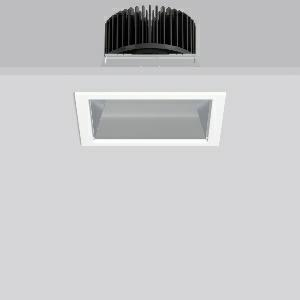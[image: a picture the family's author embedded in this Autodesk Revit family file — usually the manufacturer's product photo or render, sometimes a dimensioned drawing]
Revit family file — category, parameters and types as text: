
# Revit family: quardo_901705_002_1_76_2dd2
name_source: partatom
category: Lighting Fixtures
units: mm (PartAtom-declared; Revit-internal decimal feet)

## family parameters
Cut with Voids When Loaded = No
Host = Face
Light Source = No
Part Type = Normal
Room Calculation Point = No
Round Connector Dimension = Use Diameter
Shared = No

## types (1)
- QUARDO (1 x LED Modul 840, 2600 lm, 4000)
    Apparent Load = 19 VA
    CIE Flux Codes = 80 100 100 100 100
    Color Rendering = 80
    Color Temperature = 4000
    Default Elevation = 1800 mm
    Description = Series: QUARDO
High-quality recessed downlight with square luminous surface. Recessed mounting frame: die-cast aluminium, powder-coated. Mounting bracket: galvanised sheet steel. Reflector: aluminium, highly polished anodised finish. Ceiling installation with spring system. Including separate LED converter with connecting cable 600 mm. Through-wiring box (5 pole) available as accessory. 
Colour: traffic white, matt (RAL 9016)
Length: 176 mm
Width: 176 mm
Height: 4 mm
Cut-out length: 165 mm
Cut-out width: 165 mm
Recess height: 150 mm
Luminaire: recess height: 145 mm
Lamp: LED
Socket: without socket
Colour temperature: 4000K
Colour rendering index (CRI): 85
System power: 19 W
Rated luminous flux: 2600 lm
Luminous efficiency: 137 lm/W
Control gear: Converter, dimmable, DALI
Protection class: II
Type of protection: IP 20
    Height = 0 mm  [stored 0 ft]
    Lamp = 1 x LED Modul 840
    Lamp Light Flux = 2600 lm
    Lamp count = 1
    Length = 176 mm
    Lifetime = 50000 h
    Luminous efficacy = 137 lm/W
    Manufacturer = RZB
    ModVariant = No
    Model = 901705.002.1.76
    Mounting Place = Ceiling
    Mounting Type = Recessed
    Number of Poles = 1
    OnlyDefault = Yes
    Power Factor = 1
    Product Name = QUARDO
    Product group = Recessed downlights
    ProductGroupID = 402
    Protection Class = Protection class II
    Protection Degree = IP 20
    RLX_Detail_Level = 1
    RLX_Emergency_Light_Flux = 0 lm
    RLX_Emergency_Type = 0
    RLX_Emergency_Type_DB = No
    RlxData = <blob elided: 29337 chars, md5=5d1d8fd2>
    Socket = socket
    Standby Power = 0 W
    System Light Flux = 2600 lm
    System Power = 19 W
    Type Comments = Product without accessories
    Type Image = 901705.002.jpg
    URL = http://relux.com
    VarID = ---
    Voltage = 230 V
    Voltage Range = 220-240 V
    Weight = 0.00 kg
    Width = 176 mm

note: [stored X ft] marks values corroborated as IEEE doubles in the binary element streams (Revit-internal decimal feet)

## geometry (parser evidence)
native form markers: Blend x4, Sweep x10
no freeform markers — native parametric forms only
